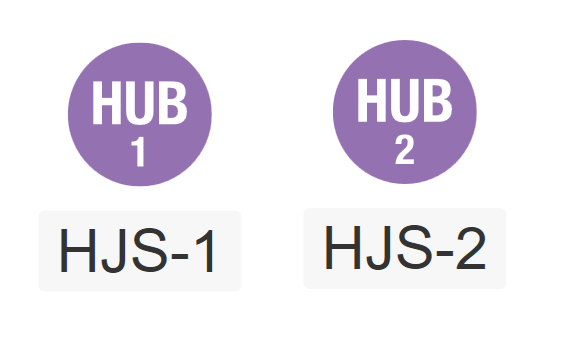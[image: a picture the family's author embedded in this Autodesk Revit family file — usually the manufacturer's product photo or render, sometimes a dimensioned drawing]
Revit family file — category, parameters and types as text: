
# Revit family: CSensor-Lutron-Ceiling-Vive_Series-HJS-2-FM
name_source: partatom
category: Lighting Devices
units: mm (PartAtom-declared; Revit-internal decimal feet)

## family parameters
Cut with Voids When Loaded = No
Host = Face
Maintain Annotation Orientation = Yes
OmniClass Number = 23.85.80.11.27
OmniClass Title = Lighting Controls
Part Type = Normal
Room Calculation Point = No
Round Connector Dimension = Use Diameter
Shared = No

## types (1)
- HJS-2-FM
    Apparent Load = 0 VA
    Assembly Code = D5030800
    Cost = 0 $
    Coverage = 15836.00 SF
    Coverage Area = 360˚ coverage from 71 ft (22 m)
    Coverage Range = 71 ft (22 m)
    Coverge Radius = 71' - 0"
    Default Elevation = 0' - 0"
    Depth = 0' - 4 39/128"
    Description = Vive hub, flush-mount adapter and power supply
    Finish = Plastic - Lutron - White Gloss
    Instruction Sheet Link = https://assets.lutron.com
    Keynote = Division 11
    Length = 0' - 6 103/128"
    Load Classification = Other
    Manufacturer = Lutron Electronics Co., Inc
    Manufacturer Fax Number = 610-282-1243
    Maximum Operating Temperature = 104 °F
    Minimum Operating Temperature = 32 °F
    Model = HJS-2-FM
    Performance URL = https://www.lutron.com
    Product Documentation Link = https://assets.lutron.com
    Product Name = Premium Vive hub with BACnet
    Product Page URL = https://commercial.lutron.com
    Sensor Material = Plastic - Lutron - White Gloss
    Sensor Type = Occupancy/Vacancy
    Series = Vive Series
    URL = http://www.lutron.com
    Version = 2021 - v1.0a
    Video Link = https://www.youtube.com
    Voltage = 120 V
    Voltage Comments = Input to power supply: 120 – 277 V~ 50/60 Hz 0.6 A • Input to Vive hub: 24 V- 350 mA
    Warranty URL = https://www.lutron.com
    Width = 0' - 6 103/128"

## geometry (parser evidence)
native form markers: Sweep x4
no freeform markers — native parametric forms only
